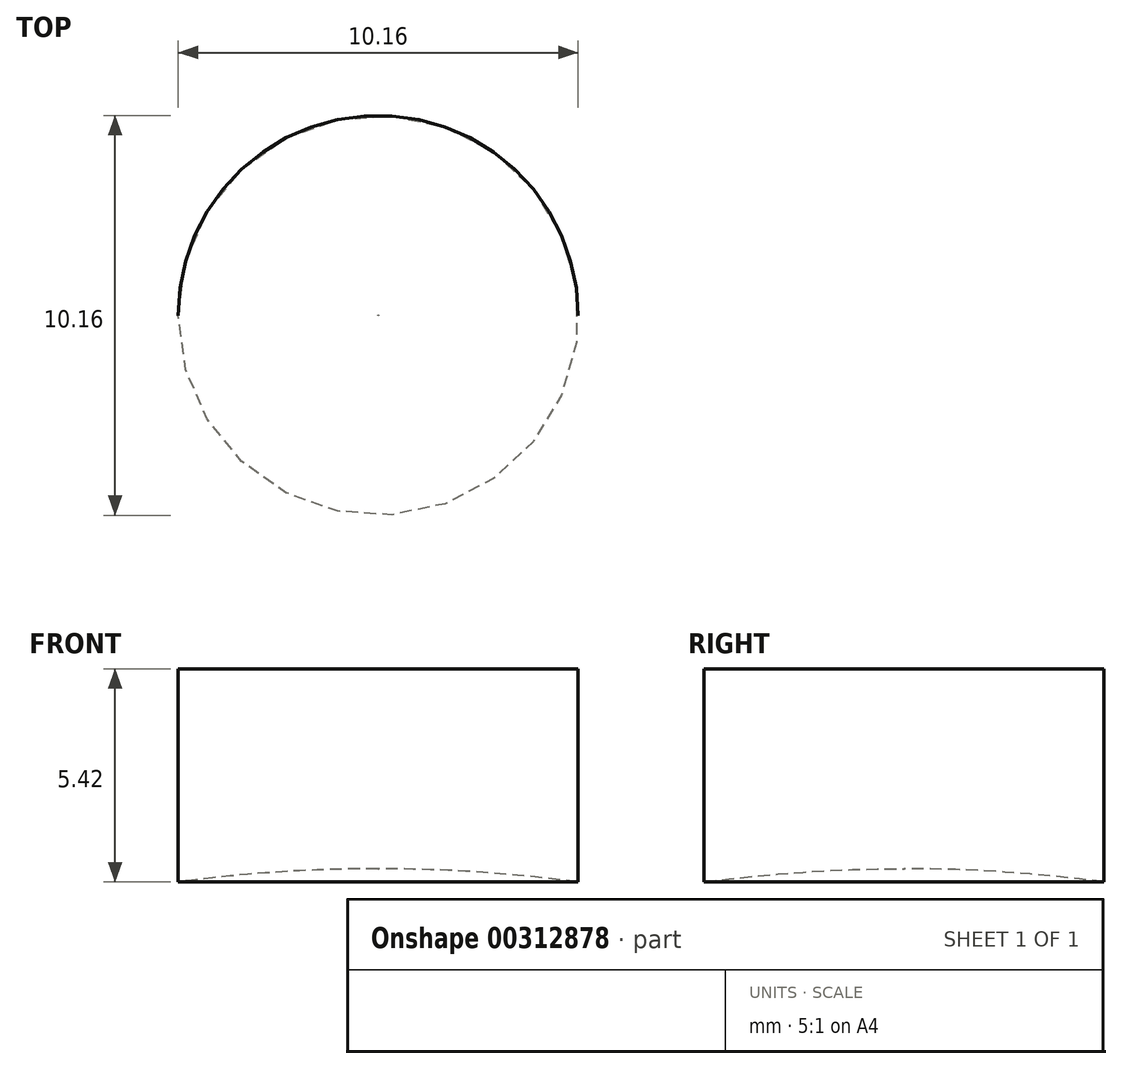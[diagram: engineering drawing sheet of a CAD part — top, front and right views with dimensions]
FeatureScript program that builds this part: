
annotation { "Feature Type Name" : "Feature", "Feature Type Description" : "" }
export const myFeature = defineFeature(function(context is Context, id is Id, definition is map)
    precondition{}
    {
        {
            var Q0;
            Q0=qCreatedBy(makeId("Front.planeOp"),FACE);
            var sketch = newSketch(context, id + "F0", { "sketchPlane" : qUnion([Q0])});
            skArc(sketch, "E0", {"start": v(0, -38.1) * mm, "mid": v(38.01, -2.55) * mm, "end": v(5.08, 37.76) * mm});
            skLineSegment(sketch, "E1", {"start": v(0, 43.18) * mm, "end": v(5.08, 43.18) * mm});
            skLineSegment(sketch, "E2", {"start": v(5.08, 43.18) * mm, "end": v(5.08, 37.76) * mm});
            skLineSegment(sketch, "E3", {"start": v(0, -38.1) * mm, "end": v(0, -32.47) * mm});
            skArc(sketch, "E4", {"start": v(0, -32.47) * mm, "mid": v(32.47, 0) * mm, "end": v(0, 32.47) * mm});
            skLineSegment(sketch, "E5.trimOffspring", {"start": v(0, 32.47) * mm, "end": v(0, 43.18) * mm});
            skSolve(sketch);
        }
        {
            var Q0;
            Q0 = qSketchRegion(id + "F0", true);
            var Q1;
            Q1=sQuery(id+"F0.wireOp",EDGE,"E3");
            revolve(context, id + "F1", {"entities" : qUnion([Q0]), "axis" : qUnion([Q1]), "revolveType" : RevolveType.FULL});
        }
        {
            var Q0;
            Q0=qCreatedBy(makeId("Front.planeOp"),FACE);
            var sketch = newSketch(context, id + "F2", { "sketchPlane" : qUnion([Q0])});
            skLineSegment(sketch, "E6", {"start": v(0, 59.58) * mm, "end": v(0, 48.93) * mm});
            skLineSegment(sketch, "E7", {"start": v(-17.27, 23.89) * mm, "end": v(-22.45, 9.2) * mm});
            skLineSegment(sketch, "E8", {"start": v(-17.27, 23.89) * mm, "end": v(-10.32, 9.36) * mm});
            skLineSegment(sketch, "E9", {"start": v(-22.45, 9.2) * mm, "end": v(-10.32, 9.36) * mm});
            skLineSegment(sketch, "E10", {"start": v(0, 5.47) * mm, "end": v(-6.33, -6.62) * mm});
            skLineSegment(sketch, "E11", {"start": v(-6.33, -6.62) * mm, "end": v(0, -6.62) * mm});
            skArc(sketch, "E12", {"start": v(-14.96, -18.7) * mm, "mid": v(-8.63, -22.97) * mm, "end": v(-1.14, -24.45) * mm});
            skLineSegment(sketch, "E13.MirrorCS", {"start": v(17.27, 23.89) * mm, "end": v(10.32, 9.36) * mm});
            skLineSegment(sketch, "E14.MirrorCS", {"start": v(17.27, 23.89) * mm, "end": v(22.45, 9.2) * mm});
            skLineSegment(sketch, "E15.MirrorCS", {"start": v(22.45, 9.2) * mm, "end": v(10.32, 9.36) * mm});
            skLineSegment(sketch, "E16.MirrorCS", {"start": v(0, 5.47) * mm, "end": v(6.33, -6.62) * mm});
            skLineSegment(sketch, "E17.MirrorCS", {"start": v(6.33, -6.62) * mm, "end": v(0, -6.62) * mm});
            skArc(sketch, "E18.MirrorCS", {"start": v(14.96, -18.7) * mm, "mid": v(8.63, -22.97) * mm, "end": v(1.14, -24.45) * mm});
            skLineSegment(sketch, "E19", {"start": v(-14.96, -18.7) * mm, "end": v(-18.52, -15.07) * mm});
            skLineSegment(sketch, "E20.MirrorCS", {"start": v(14.96, -18.7) * mm, "end": v(18.52, -15.07) * mm});
            skLineSegment(sketch, "E21", {"start": v(-18.52, -15.07) * mm, "end": v(-5.82, -15.07) * mm});
            skLineSegment(sketch, "E22", {"start": v(-5.82, -15.07) * mm, "end": v(-5.82, -18.88) * mm});
            skLineSegment(sketch, "E23", {"start": v(-5.82, -18.88) * mm, "end": v(-2, -18.88) * mm});
            skLineSegment(sketch, "E24", {"start": v(-2, -18.88) * mm, "end": v(-2, -15.07) * mm});
            skLineSegment(sketch, "E25", {"start": v(-1.14, -24.45) * mm, "end": v(1.14, -24.45) * mm});
            skLineSegment(sketch, "E26.MirrorCS", {"start": v(18.52, -15.07) * mm, "end": v(5.82, -15.07) * mm});
            skLineSegment(sketch, "E27.MirrorCS", {"start": v(5.82, -15.07) * mm, "end": v(5.82, -18.88) * mm});
            skLineSegment(sketch, "E28.MirrorCS", {"start": v(5.82, -18.88) * mm, "end": v(2, -18.88) * mm});
            skLineSegment(sketch, "E29.MirrorCS", {"start": v(2, -18.88) * mm, "end": v(2, -15.07) * mm});
            skLineSegment(sketch, "E30", {"start": v(-2, -15.07) * mm, "end": v(2, -15.07) * mm});
            skSolve(sketch);
        }
        {
            var Q0;
            Q0 = qSketchRegion(id + "F2", true);
            extrude(context, id + "F3", {"entities" : qUnion([Q0]), "operationType" : NewBodyOperationType.REMOVE, "depth" : 50.8 * mm});
        }
    });
